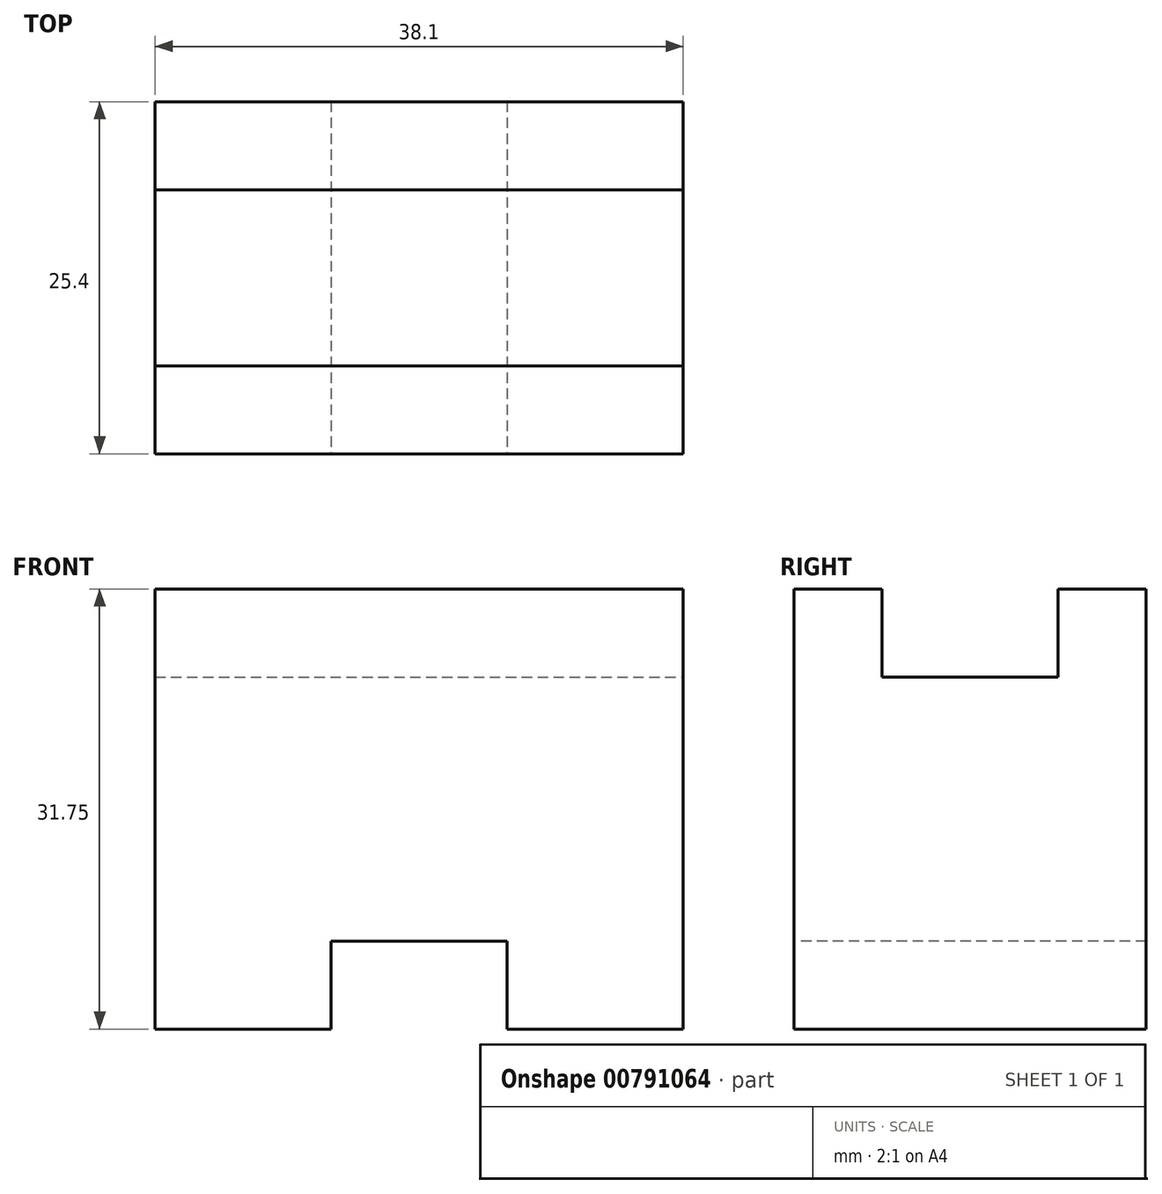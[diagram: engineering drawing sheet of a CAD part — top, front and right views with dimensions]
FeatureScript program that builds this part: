
annotation { "Feature Type Name" : "Feature", "Feature Type Description" : "" }
export const myFeature = defineFeature(function(context is Context, id is Id, definition is map)
    precondition{}
    {
        {
            var Q0;
            Q0=qCreatedBy(makeId("Front.planeOp"),FACE);
            var sketch = newSketch(context, id + "F0", { "sketchPlane" : qUnion([Q0])});
            skLineSegment(sketch, "E0", {"start": v(0, 0) * mm, "end": v(38.1, 0) * mm});
            skLineSegment(sketch, "E1", {"start": v(38.1, 0) * mm, "end": v(38.1, 31.75) * mm});
            skLineSegment(sketch, "E2", {"start": v(38.1, 31.75) * mm, "end": v(0, 31.75) * mm});
            skLineSegment(sketch, "E3", {"start": v(0, 31.75) * mm, "end": v(0, 0) * mm});
            skSolve(sketch);
        }
        {
            var Q0;
            Q0=makeQuery(id+"F0.imprint","IMPRINT",FACE,{"disambiguationData":[TD([[makeQuery(id+"F0.imprint","IMPRINT",EDGE,{"derivedFrom":sQuery(id+"F0.wireOp",EDGE,"E0")}),1.0]])]});
            extrude(context, id + "F1", {"entities" : qUnion([Q0]), "depth" : 25.4 * mm, "offsetDistance" : 25.4 * mm});
        }
        {
            var Q0;
            Q0=makeQuery(id+"F1.opExtrude","CAP_FACE",FACE,{"disambiguationData":[OSD([sQuery(id+"F0.wireOp",EDGE,"E0"),sQuery(id+"F0.wireOp",EDGE,"E1"),sQuery(id+"F0.wireOp",EDGE,"E2"),sQuery(id+"F0.wireOp",EDGE,"E3")])],"isStart":false});
            var sketch = newSketch(context, id + "F2", { "sketchPlane" : qUnion([Q0])});
            skLineSegment(sketch, "E4", {"start": v(0, 0) * mm, "end": v(12.7, 0) * mm});
            skLineSegment(sketch, "E5", {"start": v(12.7, 0) * mm, "end": v(12.7, 6.35) * mm});
            skLineSegment(sketch, "E6", {"start": v(12.7, 6.35) * mm, "end": v(25.4, 6.35) * mm});
            skLineSegment(sketch, "E7", {"start": v(25.4, 6.35) * mm, "end": v(25.4, 0) * mm});
            skLineSegment(sketch, "E8", {"start": v(25.4, 0) * mm, "end": v(38.1, 0) * mm});
            skSolve(sketch);
        }
        {
            var Q0;
            Q0=qSketchRegion(id+"F2",true);
            var Q1;
            {var subQ0=sQuery(id+"F2.wireOp",EDGE,"E5");Q1=makeQuery(id+"F2.imprint","IMPRINT",FACE,{"disambiguationData":[TD([[makeQuery(id+"F2.imprint","IMPRINT",EDGE,{"derivedFrom":subQ0}),-1.0]])]});}
            extrude(context, id + "F3", {"entities" : qUnion([Q0, Q1]), "operationType" : NewBodyOperationType.REMOVE, "oppositeDirection" : true, "depth" : 25.4 * mm, "offsetDistance" : 25.4 * mm});
        }
        {
            var Q0;
            Q0=makeQuery(id+"F1.opExtrude","SWEPT_FACE",FACE,{"disambiguationData":[OSD([sQuery(id+"F0.wireOp",EDGE,"E1")])]});
            var sketch = newSketch(context, id + "F4", { "sketchPlane" : qUnion([Q0])});
            skLineSegment(sketch, "E9", {"start": v(-25.4, 31.75) * mm, "end": v(-19.05, 31.75) * mm});
            skLineSegment(sketch, "E10", {"start": v(-19.05, 31.75) * mm, "end": v(-19.05, 25.4) * mm});
            skLineSegment(sketch, "E11", {"start": v(-19.05, 25.4) * mm, "end": v(-6.35, 25.4) * mm});
            skLineSegment(sketch, "E12", {"start": v(-6.35, 25.4) * mm, "end": v(-6.35, 31.75) * mm});
            skLineSegment(sketch, "E13", {"start": v(-6.35, 31.75) * mm, "end": v(0, 31.75) * mm});
            skSolve(sketch);
        }
        {
            var Q0;
            Q0=qSketchRegion(id+"F4",true);
            var Q1;
            {var subQ0=sQuery(id+"F4.wireOp",EDGE,"E10");Q1=makeQuery(id+"F4.imprint","IMPRINT",FACE,{"disambiguationData":[TD([[makeQuery(id+"F4.imprint","IMPRINT",EDGE,{"derivedFrom":subQ0}),1.0]])]});}
            extrude(context, id + "F5", {"entities" : qUnion([Q0, Q1]), "operationType" : NewBodyOperationType.REMOVE, "oppositeDirection" : true, "depth" : 38.1 * mm, "offsetDistance" : 25.4 * mm});
        }
    });
